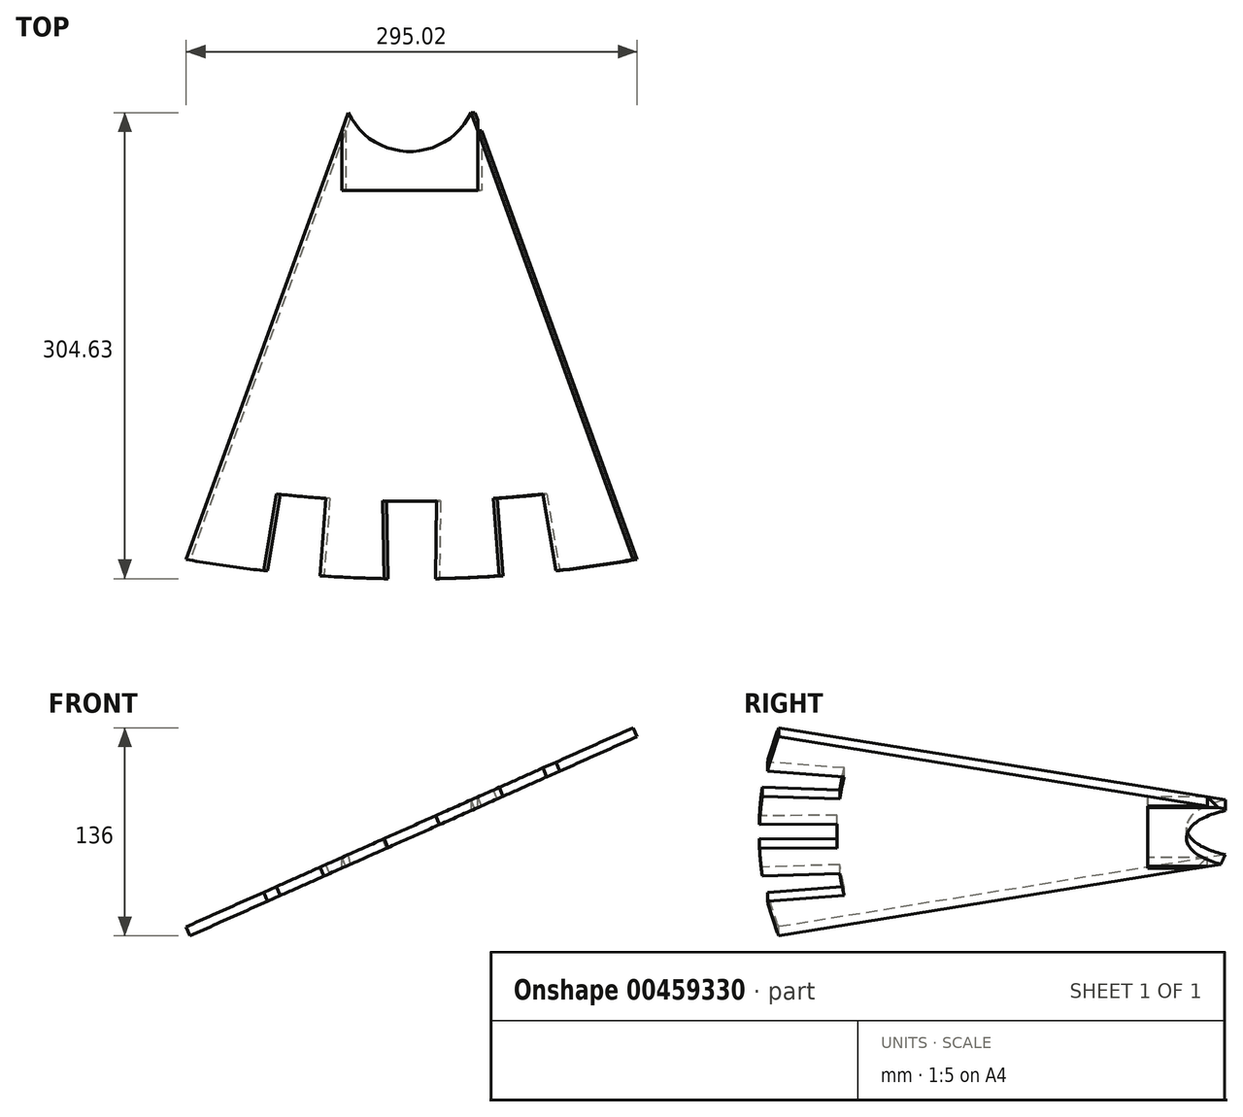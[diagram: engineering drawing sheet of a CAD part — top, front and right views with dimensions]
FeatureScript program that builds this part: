
annotation { "Feature Type Name" : "Feature", "Feature Type Description" : "" }
export const myFeature = defineFeature(function(context is Context, id is Id, definition is map)
    precondition{}
    {
        {
            var Q0;
            Q0=qCreatedBy(makeId("Top.planeOp"),FACE);
            var sketch = newSketch(context, id + "F0", { "sketchPlane" : qUnion([Q0])});
            skCircle(sketch, "E0", {"center": v(0, 0) * mm, "radius": 44.45 * mm});
            skSolve(sketch);
        }
        {
            var Q0;
            Q0=makeQuery(id+"F0.imprint","IMPRINT",FACE,{"disambiguationData":[TD([[makeQuery(id+"F0.imprint","IMPRINT",EDGE,{"derivedFrom":sQuery(id+"F0.wireOp",EDGE,"E0")}),1.0]])]});
            extrude(context, id + "F1", {"entities" : qUnion([Q0]), "depth" : 254 * mm, "offsetDistance" : 25.4 * mm});
        }
        {
            var Q0;
            Q0=qCreatedBy(makeId("Front.planeOp"),FACE);
            cPlane(context, id + "F2", {"entities" : qUnion([Q0]), "cplaneType" : CPlaneType.OFFSET, "offset" : 44.45 * mm, "width" : 152.4 * mm, "height" : 152.4 * mm});
        }
        {
            var Q0;
            Q0=qCreatedBy(id+"F2.planeOp",FACE);
            var sketch = newSketch(context, id + "F3", { "sketchPlane" : qUnion([Q0])});
            skLineSegment(sketch, "E1", {"start": v(-44.45, 0) * mm, "end": v(-44.45, 254) * mm});
            skLineSegment(sketch, "E2", {"start": v(44.45, 254) * mm, "end": v(44.45, 0) * mm});
            skLineSegment(sketch, "E3.0", {"start": v(-44.45, 254) * mm, "end": v(44.45, 254) * mm});
            skLineSegment(sketch, "E4", {"start": v(-44.45, 136.13) * mm, "end": v(44.45, 175.71) * mm});
            skLineSegment(sketch, "E5.0", {"start": v(-44.45, 129.18) * mm, "end": v(44.45, 168.76) * mm});
            skLineSegment(sketch, "E6", {"start": v(-44.45, 136.13) * mm, "end": v(-44.45, 129.18) * mm});
            skLineSegment(sketch, "E7", {"start": v(44.45, 175.71) * mm, "end": v(44.45, 168.76) * mm});
            skSolve(sketch);
        }
        {
            var Q0;
            {var subQ0=sQuery(id+"F3.wireOp",EDGE,"E4");Q0=makeQuery(id+"F3.imprint","IMPRINT",FACE,{"disambiguationData":[TD([[makeQuery(id+"F3.imprint","IMPRINT",EDGE,{"derivedFrom":subQ0}),-1.0]])]});}
            extrude(context, id + "F4", {"entities" : qUnion([Q0]), "operationType" : NewBodyOperationType.ADD, "oppositeDirection" : true, "depth" : 25.4 * mm, "offsetDistance" : 25.4 * mm});
        }
        {
            var Q0;
            Q0=makeQuery(id+"F4.opExtrude","CAP_FACE",FACE,{"disambiguationData":[OSD([sQuery(id+"F3.wireOp",EDGE,"E1"),sQuery(id+"F3.wireOp",EDGE,"E2"),sQuery(id+"F3.wireOp",EDGE,"E4"),sQuery(id+"F3.wireOp",EDGE,"E5.0")])],"isStart":true});
            extrude(context, id + "F5", {"entities" : qUnion([Q0]), "operationType" : NewBodyOperationType.ADD, "depth" : 25.4 * mm, "offsetDistance" : 25.4 * mm});
        }
        {
            var Q0;
            Q0=makeQuery(id+"F1.opExtrude","CAP_FACE",FACE,{"disambiguationData":[OSD([sQuery(id+"F0.wireOp",EDGE,"E0")])],"isStart":false});
            extrude(context, id + "F6", {"entities" : qUnion([Q0]), "operationType" : NewBodyOperationType.REMOVE, "oppositeDirection" : true, "depth" : 254 * mm, "offsetDistance" : 25.4 * mm});
        }
        {
            var Q0;
            {var subQ0=sQuery(id+"F3.wireOp",EDGE,"E4");var subQ1=sQuery(id+"F3.wireOp",EDGE,"E2");var subQ3=sQuery(id+"F3.wireOp",EDGE,"E1");var subQ7=makeQuery(id+"F4.opExtrude","SWEPT_FACE",FACE,{"disambiguationData":[OSD([subQ0])]});Q0=makeQuery(id+"F5.boolean.opBoolean","MERGE",FACE,{"derivedFrom":[makeQuery(id+"F4.boolean.opBoolean","SPLIT",FACE,{"disambiguationData":[TD([makeQuery(id+"F4.opExtrude","SWEPT_FACE",FACE,{"disambiguationData":[OSD([subQ3])]})])],"derivedFrom":subQ7}),makeQuery(id+"F4.boolean.opBoolean","SPLIT",FACE,{"disambiguationData":[TD([makeQuery(id+"F4.opExtrude","SWEPT_FACE",FACE,{"disambiguationData":[OSD([subQ1])]})])],"derivedFrom":subQ7}),makeQuery(id+"F5.opExtrude","SWEPT_FACE",FACE,{"disambiguationData":[OSD([subQ0])]})]});}
            var sketch = newSketch(context, id + "F7", { "sketchPlane" : qUnion([Q0])});
            skLineSegment(sketch, "E8", {"start": v(63.42, -44.45) * mm, "end": v(63.42, -323.85) * mm});
            skLineSegment(sketch, "E9", {"start": v(63.42, -323.85) * mm, "end": v(228.52, -323.85) * mm});
            skLineSegment(sketch, "E10", {"start": v(63.42, -323.85) * mm, "end": v(-101.68, -323.85) * mm});
            skLineSegment(sketch, "E11", {"start": v(19.46, -19.05) * mm, "end": v(-101.68, -323.85) * mm});
            skLineSegment(sketch, "E12", {"start": v(107.38, -19.05) * mm, "end": v(228.52, -323.85) * mm});
            skLineSegment(sketch, "E13", {"start": v(-101.68, -323.85) * mm, "end": v(-101.68, -298.45) * mm});
            skLineSegment(sketch, "E14", {"start": v(-91.59, -298.45) * mm, "end": v(218.42, -298.45) * mm});
            skLineSegment(sketch, "E15", {"start": v(-96.63, -311.15) * mm, "end": v(223.47, -311.15) * mm});
            skPoint(sketch, "E15.startSnap0", {"position": v(-101.68, -311.15) * mm});
            skArc(sketch, "E16", {"start": v(-96.63, -311.15) * mm, "mid": v(63.42, -323.85) * mm, "end": v(223.47, -311.15) * mm});
            skArc(sketch, "E17.0", {"start": v(-77.38, -262.71) * mm, "mid": v(63.42, -273.05) * mm, "end": v(204.22, -262.71) * mm});
            skLineSegment(sketch, "E18", {"start": v(-32, -268.32) * mm, "end": v(-41.23, -318.44) * mm});
            skLineSegment(sketch, "E19", {"start": v(3.44, -271.18) * mm, "end": v(-0.73, -321.82) * mm});
            skLineSegment(sketch, "E20", {"start": v(44.04, -272.86) * mm, "end": v(44.95, -323.68) * mm});
            skLineSegment(sketch, "E21", {"start": v(82.68, -272.86) * mm, "end": v(81.89, -323.68) * mm});
            skLineSegment(sketch, "E22", {"start": v(123.29, -271.19) * mm, "end": v(127.57, -321.82) * mm});
            skLineSegment(sketch, "E23", {"start": v(158.85, -268.32) * mm, "end": v(168.07, -318.44) * mm});
            skSolve(sketch);
        }
        {
            var Q0;
            {var subQ0=sQuery(id+"F7.wireOp",EDGE,"E17.0");var subQ2=sQuery(id+"F7.wireOp",EDGE,"E8");var subQ3=makeQuery(id+"F7.imprint","INTERSECT",VERTEX,{"derivedFrom":[subQ2,subQ0]});Q0=makeQuery(id+"F7.imprint","IMPRINT",FACE,{"disambiguationData":[TD([[makeQuery(id+"F7.imprint","IMPRINT",EDGE,{"disambiguationData":[TD([[subQ3,1.0]])],"derivedFrom":subQ2}),1.0]])]});}
            var Q1;
            {var subQ0=sQuery(id+"F7.wireOp",EDGE,"E17.0");var subQ9=sQuery(id+"F7.wireOp",EDGE,"E8");var subQ10=makeQuery(id+"F7.imprint","INTERSECT",VERTEX,{"derivedFrom":[subQ9,subQ0]});Q1=makeQuery(id+"F7.imprint","IMPRINT",FACE,{"disambiguationData":[TD([[makeQuery(id+"F7.imprint","IMPRINT",EDGE,{"disambiguationData":[TD([[subQ10,1.0]])],"derivedFrom":subQ9}),-1.0]])]});}
            var Q2;
            {var subQ0=sQuery(id+"F7.wireOp",EDGE,"E14");var subQ1=sQuery(id+"F7.wireOp",EDGE,"E11");var subQ2=makeQuery(id+"F7.imprint","INTERSECT",VERTEX,{"derivedFrom":[subQ1,subQ0]});Q2=makeQuery(id+"F7.imprint","IMPRINT",FACE,{"disambiguationData":[TD([[makeQuery(id+"F7.imprint","IMPRINT",EDGE,{"disambiguationData":[TD([[subQ2,1.0]])],"derivedFrom":subQ1}),1.0]])]});}
            var Q3;
            {var subQ0=sQuery(id+"F7.wireOp",EDGE,"E14");var subQ1=sQuery(id+"F7.wireOp",EDGE,"E11");var subQ2=makeQuery(id+"F7.imprint","INTERSECT",VERTEX,{"derivedFrom":[subQ1,subQ0]});Q3=makeQuery(id+"F7.imprint","IMPRINT",FACE,{"disambiguationData":[TD([[makeQuery(id+"F7.imprint","IMPRINT",EDGE,{"disambiguationData":[TD([[subQ2,-1.0]])],"derivedFrom":subQ0}),-1.0]])]});}
            var Q4;
            {var subQ0=sQuery(id+"F7.wireOp",EDGE,"E16");var subQ3=sQuery(id+"F7.wireOp",EDGE,"E18");var subQ5=makeQuery(id+"F7.imprint","INTERSECT",VERTEX,{"derivedFrom":[subQ0,subQ3]});Q4=makeQuery(id+"F7.imprint","IMPRINT",FACE,{"disambiguationData":[TD([[makeQuery(id+"F7.imprint","IMPRINT",EDGE,{"disambiguationData":[TD([[subQ5,1.0]])],"derivedFrom":subQ3}),-1.0]])]});}
            var Q5;
            {var subQ0=sQuery(id+"F7.wireOp",EDGE,"E19");var subQ1=sQuery(id+"F7.wireOp",EDGE,"E14");var subQ2=makeQuery(id+"F7.imprint","INTERSECT",VERTEX,{"derivedFrom":[subQ1,subQ0]});Q5=makeQuery(id+"F7.imprint","IMPRINT",FACE,{"disambiguationData":[TD([[makeQuery(id+"F7.imprint","IMPRINT",EDGE,{"disambiguationData":[TD([[subQ2,-1.0]])],"derivedFrom":subQ1}),1.0]])]});}
            var Q6;
            {var subQ0=sQuery(id+"F7.wireOp",EDGE,"E19");var subQ1=sQuery(id+"F7.wireOp",EDGE,"E14");var subQ2=makeQuery(id+"F7.imprint","INTERSECT",VERTEX,{"derivedFrom":[subQ1,subQ0]});Q6=makeQuery(id+"F7.imprint","IMPRINT",FACE,{"disambiguationData":[TD([[makeQuery(id+"F7.imprint","IMPRINT",EDGE,{"disambiguationData":[TD([[subQ2,-1.0]])],"derivedFrom":subQ1}),-1.0]])]});}
            var Q7;
            {var subQ0=sQuery(id+"F7.wireOp",EDGE,"E19");var subQ1=sQuery(id+"F7.wireOp",EDGE,"E15");var subQ2=makeQuery(id+"F7.imprint","INTERSECT",VERTEX,{"derivedFrom":[subQ1,subQ0]});Q7=makeQuery(id+"F7.imprint","IMPRINT",FACE,{"disambiguationData":[TD([[makeQuery(id+"F7.imprint","IMPRINT",EDGE,{"disambiguationData":[TD([[subQ2,-1.0]])],"derivedFrom":subQ1}),-1.0]])]});}
            var Q8;
            {var subQ0=sQuery(id+"F7.wireOp",EDGE,"E21");var subQ1=sQuery(id+"F7.wireOp",EDGE,"E14");var subQ2=makeQuery(id+"F7.imprint","INTERSECT",VERTEX,{"derivedFrom":[subQ1,subQ0]});Q8=makeQuery(id+"F7.imprint","IMPRINT",FACE,{"disambiguationData":[TD([[makeQuery(id+"F7.imprint","IMPRINT",EDGE,{"disambiguationData":[TD([[subQ2,-1.0]])],"derivedFrom":subQ1}),1.0]])]});}
            var Q9;
            {var subQ0=sQuery(id+"F7.wireOp",EDGE,"E21");var subQ1=sQuery(id+"F7.wireOp",EDGE,"E14");var subQ2=makeQuery(id+"F7.imprint","INTERSECT",VERTEX,{"derivedFrom":[subQ1,subQ0]});Q9=makeQuery(id+"F7.imprint","IMPRINT",FACE,{"disambiguationData":[TD([[makeQuery(id+"F7.imprint","IMPRINT",EDGE,{"disambiguationData":[TD([[subQ2,-1.0]])],"derivedFrom":subQ1}),-1.0]])]});}
            var Q10;
            {var subQ0=sQuery(id+"F7.wireOp",EDGE,"E21");var subQ1=sQuery(id+"F7.wireOp",EDGE,"E15");var subQ2=makeQuery(id+"F7.imprint","INTERSECT",VERTEX,{"derivedFrom":[subQ1,subQ0]});Q10=makeQuery(id+"F7.imprint","IMPRINT",FACE,{"disambiguationData":[TD([[makeQuery(id+"F7.imprint","IMPRINT",EDGE,{"disambiguationData":[TD([[subQ2,-1.0]])],"derivedFrom":subQ1}),-1.0]])]});}
            var Q11;
            {var subQ0=sQuery(id+"F7.wireOp",EDGE,"E17.0");var subQ1=sQuery(id+"F7.wireOp",EDGE,"E12");var subQ2=makeQuery(id+"F7.imprint","INTERSECT",VERTEX,{"derivedFrom":[subQ1,subQ0]});Q11=makeQuery(id+"F7.imprint","IMPRINT",FACE,{"disambiguationData":[TD([[makeQuery(id+"F7.imprint","IMPRINT",EDGE,{"disambiguationData":[TD([[subQ2,-1.0]])],"derivedFrom":subQ1}),-1.0]])]});}
            var Q12;
            {var subQ1=sQuery(id+"F7.wireOp",EDGE,"E12");var subQ3=sQuery(id+"F7.wireOp",EDGE,"E14");var subQ4=makeQuery(id+"F7.imprint","INTERSECT",VERTEX,{"derivedFrom":[subQ1,subQ3]});Q12=makeQuery(id+"F7.imprint","IMPRINT",FACE,{"disambiguationData":[TD([[makeQuery(id+"F7.imprint","IMPRINT",EDGE,{"disambiguationData":[TD([[subQ4,1.0]])],"derivedFrom":subQ3}),-1.0]])]});}
            var Q13;
            {var subQ0=sQuery(id+"F7.wireOp",EDGE,"E23");var subQ1=sQuery(id+"F7.wireOp",EDGE,"E15");var subQ2=makeQuery(id+"F7.imprint","INTERSECT",VERTEX,{"derivedFrom":[subQ1,subQ0]});Q13=makeQuery(id+"F7.imprint","IMPRINT",FACE,{"disambiguationData":[TD([[makeQuery(id+"F7.imprint","IMPRINT",EDGE,{"disambiguationData":[TD([[subQ2,-1.0]])],"derivedFrom":subQ0}),1.0]])]});}
            extrude(context, id + "F8", {"entities" : qUnion([Q0, Q1, Q2, Q3, Q4, Q5, Q6, Q7, Q8, Q9, Q10, Q11, Q12, Q13]), "oppositeDirection" : true, "depth" : 6.35 * mm, "offsetDistance" : 25.4 * mm});
        }
        {
            var Q0;
            {var subQ0=sQuery(id+"F7.wireOp",EDGE,"E17.0");var subQ9=sQuery(id+"F7.wireOp",EDGE,"E8");var subQ10=makeQuery(id+"F7.imprint","INTERSECT",VERTEX,{"derivedFrom":[subQ9,subQ0]});Q0=makeQuery(id+"F7.imprint","IMPRINT",FACE,{"disambiguationData":[TD([[makeQuery(id+"F7.imprint","IMPRINT",EDGE,{"disambiguationData":[TD([[subQ10,1.0]])],"derivedFrom":subQ9}),-1.0]])]});}
            var sketch = newSketch(context, id + "F9", { "sketchPlane" : qUnion([Q0])});
            skLineSegment(sketch, "E24.0", {"start": v(19.46, -19.05) * mm, "end": v(-101.68, -323.85) * mm});
            skLineSegment(sketch, "E25", {"start": v(19.46, -19.05) * mm, "end": v(22.84, -15.42) * mm});
            skLineSegment(sketch, "E26", {"start": v(22.84, -15.42) * mm, "end": v(-1.88, -15.42) * mm});
            skLineSegment(sketch, "E27", {"start": v(-1.88, -15.42) * mm, "end": v(4.73, -56.12) * mm});
            skSolve(sketch);
        }
        {
            var Q0;
            {var subQ0=sQuery(id+"F9.wireOp",EDGE,"E25");Q0=makeQuery(id+"F9.imprint","IMPRINT",FACE,{"disambiguationData":[TD([[makeQuery(id+"F9.imprint","IMPRINT",EDGE,{"derivedFrom":subQ0}),1.0]])]});}
            extrude(context, id + "F10", {"entities" : qUnion([Q0]), "operationType" : NewBodyOperationType.REMOVE, "oppositeDirection" : true, "depth" : 6.35 * mm, "offsetDistance" : 25.4 * mm});
        }
        {
            var Q0;
            {var subQ0=sQuery(id+"F7.wireOp",EDGE,"E17.0");var subQ2=sQuery(id+"F7.wireOp",EDGE,"E8");var subQ3=makeQuery(id+"F7.imprint","INTERSECT",VERTEX,{"derivedFrom":[subQ2,subQ0]});Q0=makeQuery(id+"F7.imprint","IMPRINT",FACE,{"disambiguationData":[TD([[makeQuery(id+"F7.imprint","IMPRINT",EDGE,{"disambiguationData":[TD([[subQ3,1.0]])],"derivedFrom":subQ2}),1.0]])]});}
            var sketch = newSketch(context, id + "F11", { "sketchPlane" : qUnion([Q0])});
            skLineSegment(sketch, "E28.0", {"start": v(107.38, -19.05) * mm, "end": v(228.52, -323.85) * mm});
            skLineSegment(sketch, "E29", {"start": v(107.38, -19.05) * mm, "end": v(107.38, -7.57) * mm});
            skLineSegment(sketch, "E30", {"start": v(107.38, -7.57) * mm, "end": v(130.15, -10.12) * mm});
            skLineSegment(sketch, "E31", {"start": v(130.15, -10.12) * mm, "end": v(116.4, -41.75) * mm});
            skSolve(sketch);
        }
        {
            var Q0;
            {var subQ0=sQuery(id+"F11.wireOp",EDGE,"E29");Q0=makeQuery(id+"F11.imprint","IMPRINT",FACE,{"disambiguationData":[TD([[makeQuery(id+"F11.imprint","IMPRINT",EDGE,{"derivedFrom":subQ0}),-1.0]])]});}
            extrude(context, id + "F12", {"entities" : qUnion([Q0]), "operationType" : NewBodyOperationType.REMOVE, "oppositeDirection" : true, "depth" : 6.35 * mm, "offsetDistance" : 25.4 * mm});
        }
    });
